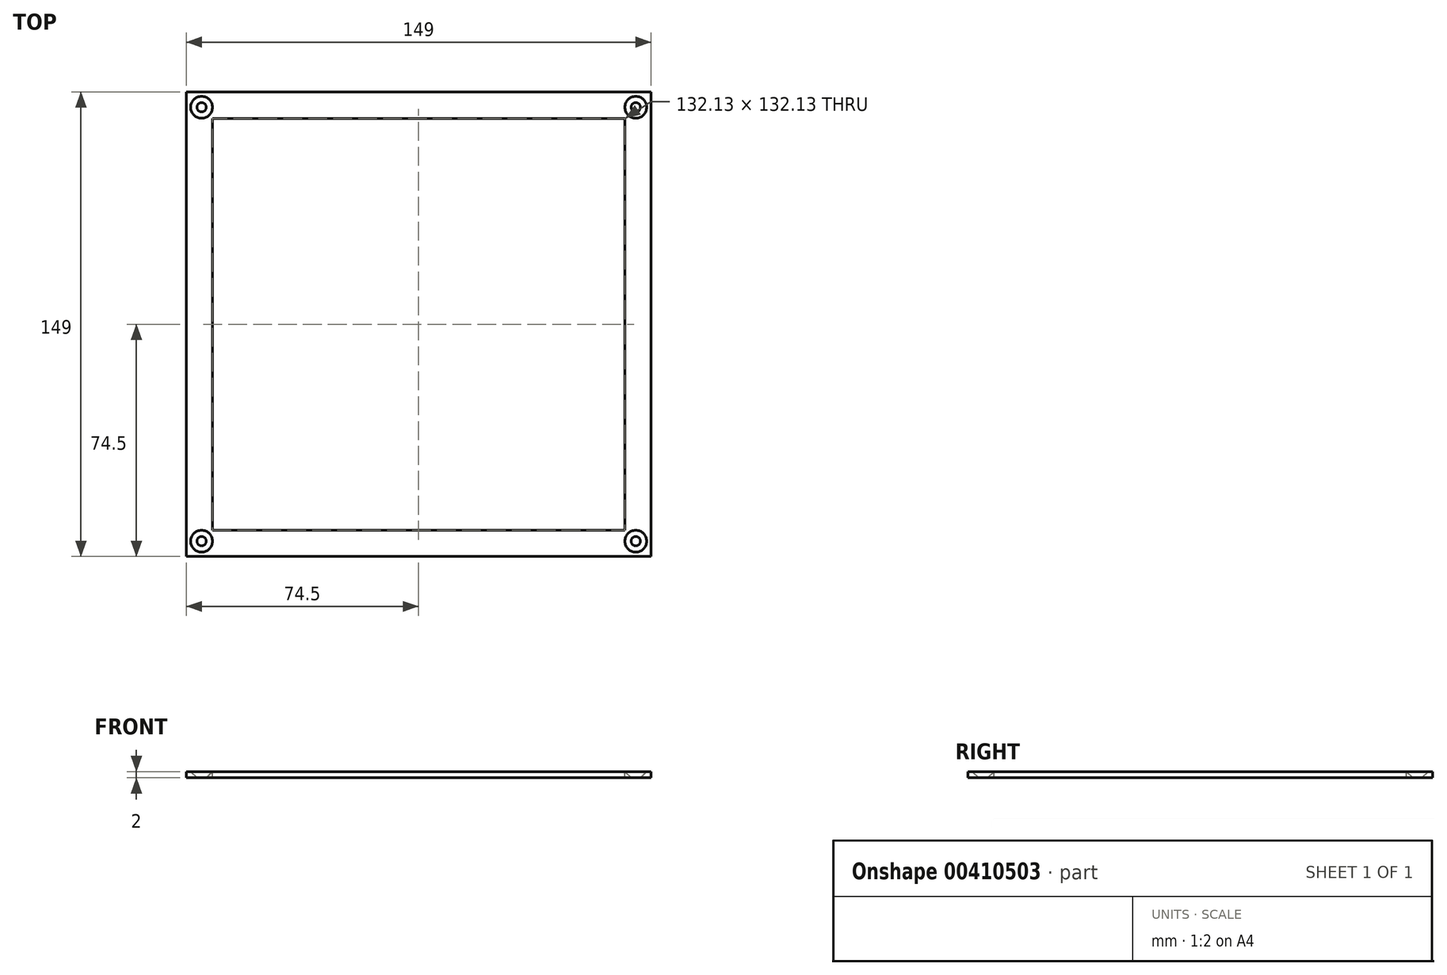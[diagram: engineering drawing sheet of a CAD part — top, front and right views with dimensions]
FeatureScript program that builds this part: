
annotation { "Feature Type Name" : "Feature", "Feature Type Description" : "" }
export const myFeature = defineFeature(function(context is Context, id is Id, definition is map)
    precondition{}
    {
        {
            var Q0;
            Q0=qCreatedBy(makeId("Top.planeOp"),FACE);
            var sketch = newSketch(context, id + "F0", { "sketchPlane" : qUnion([Q0])});
            skLineSegment(sketch, "E0.bottom", {"start": v(60.5, 60.5) * mm, "end": v(-60.5, 60.5) * mm});
            skLineSegment(sketch, "E0.top", {"start": v(60.5, -60.5) * mm, "end": v(-60.5, -60.5) * mm});
            skLineSegment(sketch, "E0.left", {"start": v(60.5, 60.5) * mm, "end": v(60.5, -60.5) * mm});
            skLineSegment(sketch, "E0.right", {"start": v(-60.5, 60.5) * mm, "end": v(-60.5, -60.5) * mm});
            skLineSegment(sketch, "E1.0", {"start": v(60.5, 57.5) * mm, "end": v(-60.5, 57.5) * mm});
            skLineSegment(sketch, "E2.0", {"start": v(57.5, 60.5) * mm, "end": v(57.5, -60.5) * mm});
            skLineSegment(sketch, "E3.0", {"start": v(60.5, -57.5) * mm, "end": v(-60.5, -57.5) * mm});
            skLineSegment(sketch, "E4.0", {"start": v(-57.5, 60.5) * mm, "end": v(-57.5, -60.5) * mm});
            skLineSegment(sketch, "E5.0", {"start": v(60.5, 74.5) * mm, "end": v(-60.5, 74.5) * mm});
            skLineSegment(sketch, "E6.0", {"start": v(60.5, -74.5) * mm, "end": v(-60.5, -74.5) * mm});
            skLineSegment(sketch, "E7.0", {"start": v(-74.5, 60.5) * mm, "end": v(-74.5, -60.5) * mm});
            skLineSegment(sketch, "E8.0", {"start": v(74.5, 60.5) * mm, "end": v(74.5, -60.5) * mm});
            skLineSegment(sketch, "E9", {"start": v(-74.5, 60.5) * mm, "end": v(-74.5, 74.5) * mm});
            skLineSegment(sketch, "E10", {"start": v(-60.5, 74.5) * mm, "end": v(-74.5, 74.5) * mm});
            skLineSegment(sketch, "E11", {"start": v(60.5, 74.5) * mm, "end": v(74.5, 74.5) * mm});
            skLineSegment(sketch, "E12", {"start": v(74.5, 60.5) * mm, "end": v(74.5, 74.5) * mm});
            skLineSegment(sketch, "E13", {"start": v(74.5, -60.5) * mm, "end": v(74.5, -74.5) * mm});
            skLineSegment(sketch, "E14", {"start": v(60.5, -74.5) * mm, "end": v(74.5, -74.5) * mm});
            skLineSegment(sketch, "E15", {"start": v(-60.5, -74.5) * mm, "end": v(-74.5, -74.5) * mm});
            skLineSegment(sketch, "E16", {"start": v(-74.5, -60.5) * mm, "end": v(-74.5, -74.5) * mm});
            skPoint(sketch, "E17.orphan", {"position": v(82.8, 74.5) * mm});
            skSolve(sketch);
        }
        {
            var Q0;
            Q0=makeQuery(id+"F0.imprint","IMPRINT",FACE,{"disambiguationData":[TD([[makeQuery(id+"F0.imprint","IMPRINT",EDGE,{"derivedFrom":sQuery(id+"F0.wireOp",EDGE,"E5.0")}),1.0]])]});
            extrude(context, id + "F1", {"entities" : qUnion([Q0]), "depth" : 5 * mm});
        }
        {
            var Q0;
            {var subQ0=sQuery(id+"F0.wireOp",EDGE,"E2.0");var subQ1=sQuery(id+"F0.wireOp",EDGE,"E0.bottom");var subQ2=makeQuery(id+"F0.imprint","INTERSECT",VERTEX,{"derivedFrom":[subQ1,subQ0]});Q0=makeQuery(id+"F0.imprint","IMPRINT",FACE,{"disambiguationData":[TD([[makeQuery(id+"F0.imprint","IMPRINT",EDGE,{"disambiguationData":[TD([[subQ2,-1.0]])],"derivedFrom":subQ1}),1.0]])]});}
            var Q1;
            {var subQ0=sQuery(id+"F0.wireOp",EDGE,"E0.left");var subQ1=sQuery(id+"F0.wireOp",EDGE,"E0.bottom");var subQ2=makeQuery(id+"F0.imprint","INTERSECT",VERTEX,{"derivedFrom":[subQ1,subQ0]});Q1=makeQuery(id+"F0.imprint","IMPRINT",FACE,{"disambiguationData":[TD([[makeQuery(id+"F0.imprint","IMPRINT",EDGE,{"disambiguationData":[TD([[subQ2,-1.0]])],"derivedFrom":subQ1}),1.0]])]});}
            var Q2;
            {var subQ0=sQuery(id+"F0.wireOp",EDGE,"E1.0");var subQ1=sQuery(id+"F0.wireOp",EDGE,"E0.left");var subQ2=makeQuery(id+"F0.imprint","INTERSECT",VERTEX,{"derivedFrom":[subQ1,subQ0]});Q2=makeQuery(id+"F0.imprint","IMPRINT",FACE,{"disambiguationData":[TD([[makeQuery(id+"F0.imprint","IMPRINT",EDGE,{"disambiguationData":[TD([[subQ2,-1.0]])],"derivedFrom":subQ1}),-1.0]])]});}
            var Q3;
            {var subQ0=sQuery(id+"F0.wireOp",EDGE,"E0.left");var subQ1=sQuery(id+"F0.wireOp",EDGE,"E0.top");var subQ2=makeQuery(id+"F0.imprint","INTERSECT",VERTEX,{"derivedFrom":[subQ1,subQ0]});Q3=makeQuery(id+"F0.imprint","IMPRINT",FACE,{"disambiguationData":[TD([[makeQuery(id+"F0.imprint","IMPRINT",EDGE,{"disambiguationData":[TD([[subQ2,-1.0]])],"derivedFrom":subQ1}),-1.0]])]});}
            var Q4;
            {var subQ0=sQuery(id+"F0.wireOp",EDGE,"E2.0");var subQ1=sQuery(id+"F0.wireOp",EDGE,"E0.top");var subQ2=makeQuery(id+"F0.imprint","INTERSECT",VERTEX,{"derivedFrom":[subQ1,subQ0]});Q4=makeQuery(id+"F0.imprint","IMPRINT",FACE,{"disambiguationData":[TD([[makeQuery(id+"F0.imprint","IMPRINT",EDGE,{"disambiguationData":[TD([[subQ2,-1.0]])],"derivedFrom":subQ1}),-1.0]])]});}
            var Q5;
            {var subQ0=sQuery(id+"F0.wireOp",EDGE,"E1.0");var subQ1=sQuery(id+"F0.wireOp",EDGE,"E0.right");var subQ2=makeQuery(id+"F0.imprint","INTERSECT",VERTEX,{"derivedFrom":[subQ1,subQ0]});Q5=makeQuery(id+"F0.imprint","IMPRINT",FACE,{"disambiguationData":[TD([[makeQuery(id+"F0.imprint","IMPRINT",EDGE,{"disambiguationData":[TD([[subQ2,-1.0]])],"derivedFrom":subQ1}),1.0]])]});}
            var Q6;
            {var subQ0=sQuery(id+"F0.wireOp",EDGE,"E0.right");var subQ1=sQuery(id+"F0.wireOp",EDGE,"E0.top");var subQ2=makeQuery(id+"F0.imprint","INTERSECT",VERTEX,{"derivedFrom":[subQ1,subQ0]});Q6=makeQuery(id+"F0.imprint","IMPRINT",FACE,{"disambiguationData":[TD([[makeQuery(id+"F0.imprint","IMPRINT",EDGE,{"disambiguationData":[TD([[subQ2,1.0]])],"derivedFrom":subQ1}),-1.0]])]});}
            var Q7;
            {var subQ0=sQuery(id+"F0.wireOp",EDGE,"E0.right");var subQ1=sQuery(id+"F0.wireOp",EDGE,"E0.bottom");var subQ2=makeQuery(id+"F0.imprint","INTERSECT",VERTEX,{"derivedFrom":[subQ1,subQ0]});Q7=makeQuery(id+"F0.imprint","IMPRINT",FACE,{"disambiguationData":[TD([[makeQuery(id+"F0.imprint","IMPRINT",EDGE,{"disambiguationData":[TD([[subQ2,1.0]])],"derivedFrom":subQ1}),1.0]])]});}
            extrude(context, id + "F2", {"entities" : qUnion([Q0, Q1, Q2, Q3, Q4, Q5, Q6, Q7]), "operationType" : NewBodyOperationType.ADD, "depth" : 2 * mm});
        }
        {
            var Q0;
            Q0=makeQuery(id+"F1.opExtrude","CAP_FACE",FACE,{"disambiguationData":[OSD([sQuery(id+"F0.wireOp",EDGE,"E0.bottom"),sQuery(id+"F0.wireOp",EDGE,"E0.top"),sQuery(id+"F0.wireOp",EDGE,"E0.left"),sQuery(id+"F0.wireOp",EDGE,"E0.right"),sQuery(id+"F0.wireOp",EDGE,"E5.0"),sQuery(id+"F0.wireOp",EDGE,"E6.0"),sQuery(id+"F0.wireOp",EDGE,"E7.0"),sQuery(id+"F0.wireOp",EDGE,"E8.0"),sQuery(id+"F0.wireOp",EDGE,"E9"),sQuery(id+"F0.wireOp",EDGE,"E10"),sQuery(id+"F0.wireOp",EDGE,"E11"),sQuery(id+"F0.wireOp",EDGE,"E12"),sQuery(id+"F0.wireOp",EDGE,"E13"),sQuery(id+"F0.wireOp",EDGE,"E14"),sQuery(id+"F0.wireOp",EDGE,"E15"),sQuery(id+"F0.wireOp",EDGE,"E16")])],"isStart":false});
            var sketch = newSketch(context, id + "F3", { "sketchPlane" : qUnion([Q0])});
            skCircle(sketch, "E18", {"center": v(42.52, 68.09) * mm, "radius": 2.5 * mm});
            skSolve(sketch);
        }
        {
            var Q0;
            Q0=makeQuery(id+"F3.imprint","IMPRINT",FACE,{"disambiguationData":[TD([[makeQuery(id+"F3.imprint","IMPRINT",EDGE,{"derivedFrom":sQuery(id+"F3.wireOp",EDGE,"E18")}),1.0]])]});
            extrude(context, id + "F4", {"entities" : qUnion([Q0]), "operationType" : NewBodyOperationType.REMOVE, "endBound" : BoundingType.UP_TO_NEXT, "oppositeDirection" : true, "depth" : 25 * mm});
        }
        {
            var Q0;
            Q0=makeQuery(id+"F1.opExtrude","CAP_FACE",FACE,{"disambiguationData":[OSD([sQuery(id+"F0.wireOp",EDGE,"E0.bottom"),sQuery(id+"F0.wireOp",EDGE,"E0.top"),sQuery(id+"F0.wireOp",EDGE,"E0.left"),sQuery(id+"F0.wireOp",EDGE,"E0.right"),sQuery(id+"F0.wireOp",EDGE,"E5.0"),sQuery(id+"F0.wireOp",EDGE,"E6.0"),sQuery(id+"F0.wireOp",EDGE,"E7.0"),sQuery(id+"F0.wireOp",EDGE,"E8.0"),sQuery(id+"F0.wireOp",EDGE,"E9"),sQuery(id+"F0.wireOp",EDGE,"E10"),sQuery(id+"F0.wireOp",EDGE,"E11"),sQuery(id+"F0.wireOp",EDGE,"E12"),sQuery(id+"F0.wireOp",EDGE,"E13"),sQuery(id+"F0.wireOp",EDGE,"E14"),sQuery(id+"F0.wireOp",EDGE,"E15"),sQuery(id+"F0.wireOp",EDGE,"E16")])],"isStart":false});
            var sketch = newSketch(context, id + "F5", { "sketchPlane" : qUnion([Q0])});
            skLineSegment(sketch, "E19.0", {"start": v(60.5, 71.5) * mm, "end": v(71.5, 71.5) * mm});
            skLineSegment(sketch, "E19.1", {"start": v(-71.5, -60.5) * mm, "end": v(-71.5, -71.5) * mm});
            skLineSegment(sketch, "E19.2", {"start": v(-71.5, 60.5) * mm, "end": v(-71.5, -60.5) * mm});
            skLineSegment(sketch, "E19.3", {"start": v(-71.5, 60.5) * mm, "end": v(-71.5, 71.5) * mm});
            skLineSegment(sketch, "E19.4", {"start": v(-60.5, 71.5) * mm, "end": v(-71.5, 71.5) * mm});
            skLineSegment(sketch, "E19.5", {"start": v(-60.5, -71.5) * mm, "end": v(-71.5, -71.5) * mm});
            skLineSegment(sketch, "E19.6", {"start": v(60.5, 71.5) * mm, "end": v(-60.5, 71.5) * mm});
            skLineSegment(sketch, "E19.7", {"start": v(60.5, -71.5) * mm, "end": v(-60.5, -71.5) * mm});
            skLineSegment(sketch, "E19.8", {"start": v(60.5, -71.5) * mm, "end": v(71.5, -71.5) * mm});
            skLineSegment(sketch, "E19.9", {"start": v(71.5, -60.5) * mm, "end": v(71.5, -71.5) * mm});
            skLineSegment(sketch, "E19.10", {"start": v(71.5, 60.5) * mm, "end": v(71.5, -60.5) * mm});
            skLineSegment(sketch, "E19.11", {"start": v(71.5, 60.5) * mm, "end": v(71.5, 71.5) * mm});
            skSolve(sketch);
        }
        {
            var Q0;
            Q0=makeQuery(id+"F5.imprint","IMPRINT",FACE,{"disambiguationData":[TD([[makeQuery(id+"F5.imprint","IMPRINT",EDGE,{"derivedFrom":sQuery(id+"F5.wireOp",EDGE,"E19.0")}),1.0]])]});
            extrude(context, id + "F6", {"entities" : qUnion([Q0]), "operationType" : NewBodyOperationType.ADD, "depth" : 35 * mm});
        }
        {
            var Q0;
            Q0=makeQuery(id+"F6.opExtrude","CAP_FACE",FACE,{"disambiguationData":[OSD([sQuery(id+"F0.wireOp",EDGE,"E5.0"),sQuery(id+"F0.wireOp",EDGE,"E6.0"),sQuery(id+"F0.wireOp",EDGE,"E7.0"),sQuery(id+"F0.wireOp",EDGE,"E8.0"),sQuery(id+"F0.wireOp",EDGE,"E9"),sQuery(id+"F0.wireOp",EDGE,"E10"),sQuery(id+"F0.wireOp",EDGE,"E11"),sQuery(id+"F0.wireOp",EDGE,"E12"),sQuery(id+"F0.wireOp",EDGE,"E13"),sQuery(id+"F0.wireOp",EDGE,"E14"),sQuery(id+"F0.wireOp",EDGE,"E15"),sQuery(id+"F0.wireOp",EDGE,"E16"),sQuery(id+"F5.wireOp",EDGE,"E19.0"),sQuery(id+"F5.wireOp",EDGE,"E19.1"),sQuery(id+"F5.wireOp",EDGE,"E19.2"),sQuery(id+"F5.wireOp",EDGE,"E19.3"),sQuery(id+"F5.wireOp",EDGE,"E19.4"),sQuery(id+"F5.wireOp",EDGE,"E19.5"),sQuery(id+"F5.wireOp",EDGE,"E19.6"),sQuery(id+"F5.wireOp",EDGE,"E19.7"),sQuery(id+"F5.wireOp",EDGE,"E19.8"),sQuery(id+"F5.wireOp",EDGE,"E19.9"),sQuery(id+"F5.wireOp",EDGE,"E19.10"),sQuery(id+"F5.wireOp",EDGE,"E19.11")])],"isStart":false});
            var sketch = newSketch(context, id + "F7", { "sketchPlane" : qUnion([Q0])});
            skCircle(sketch, "E20", {"center": v(-69.6, 69.6) * mm, "radius": 5 * mm});
            skCircle(sketch, "E21", {"center": v(-69.6, 69.6) * mm, "radius": 1.5 * mm});
            skCircle(sketch, "E22.1.0", {"center": v(-69.6, -69.6) * mm, "radius": 5 * mm});
            skCircle(sketch, "E22.1.1", {"center": v(-69.6, -69.6) * mm, "radius": 1.5 * mm});
            skCircle(sketch, "E22.2.0", {"center": v(69.6, -69.6) * mm, "radius": 5 * mm});
            skCircle(sketch, "E22.2.1", {"center": v(69.6, -69.6) * mm, "radius": 1.5 * mm});
            skCircle(sketch, "E22.3.0", {"center": v(69.6, 69.6) * mm, "radius": 5 * mm});
            skCircle(sketch, "E22.3.1", {"center": v(69.6, 69.6) * mm, "radius": 1.5 * mm});
            skPoint(sketch, "E22.center", {"position": v(0, 0) * mm});
            skSolve(sketch);
        }
        {
            var Q0;
            Q0=makeQuery(id+"F7.imprint","IMPRINT",FACE,{"disambiguationData":[TD([[makeQuery(id+"F7.imprint","IMPRINT",EDGE,{"derivedFrom":sQuery(id+"F7.wireOp",EDGE,"E21")}),-1.0]])]});
            var Q1;
            Q1=makeQuery(id+"F7.imprint","IMPRINT",FACE,{"disambiguationData":[TD([[makeQuery(id+"F7.imprint","IMPRINT",EDGE,{"derivedFrom":sQuery(id+"F7.wireOp",EDGE,"E22.3.1")}),-1.0]])]});
            var Q2;
            Q2=makeQuery(id+"F7.imprint","IMPRINT",FACE,{"disambiguationData":[TD([[makeQuery(id+"F7.imprint","IMPRINT",EDGE,{"derivedFrom":sQuery(id+"F7.wireOp",EDGE,"E22.2.1")}),-1.0]])]});
            var Q3;
            Q3=makeQuery(id+"F7.imprint","IMPRINT",FACE,{"disambiguationData":[TD([[makeQuery(id+"F7.imprint","IMPRINT",EDGE,{"derivedFrom":sQuery(id+"F7.wireOp",EDGE,"E22.1.1")}),-1.0]])]});
            extrude(context, id + "F8", {"entities" : qUnion([Q0, Q1, Q2, Q3]), "operationType" : NewBodyOperationType.ADD, "oppositeDirection" : true, "depth" : 35 * mm});
        }
        {
            var Q0;
            {var subQ0=sQuery(id+"F0.wireOp",EDGE,"E15");var subQ1=sQuery(id+"F0.wireOp",EDGE,"E14");var subQ2=sQuery(id+"F0.wireOp",EDGE,"E6.0");Q0=makeQuery(id+"F6.boolean.opBoolean","MERGE",FACE,{"derivedFrom":[makeQuery(id+"F1.opExtrude","SWEPT_FACE",FACE,{"disambiguationData":[OSD([subQ2,subQ1,subQ0])]}),makeQuery(id+"F6.opExtrude","SWEPT_FACE",FACE,{"disambiguationData":[OSD([subQ2,subQ1,subQ0])]})]});}
            var sketch = newSketch(context, id + "F9", { "sketchPlane" : qUnion([Q0])});
            skLineSegment(sketch, "E23.0", {"start": v(74.5, 38) * mm, "end": v(-74.5, 38) * mm});
            skLineSegment(sketch, "E24", {"start": v(-74.5, 38) * mm, "end": v(-74.5, -12.58) * mm});
            skLineSegment(sketch, "E25", {"start": v(-74.5, -12.58) * mm, "end": v(74.5, -12.58) * mm});
            skLineSegment(sketch, "E26", {"start": v(74.5, -12.58) * mm, "end": v(74.5, 38) * mm});
            skSolve(sketch);
        }
        {
            var Q0;
            Q0 = qSketchRegion(id + "F9", true);
            extrude(context, id + "F10", {"entities" : qUnion([Q0]), "operationType" : NewBodyOperationType.REMOVE, "oppositeDirection" : true, "depth" : 200 * mm});
        }
        {
            var Q0;
            {var subQ0=sQuery(id+"F5.wireOp",EDGE,"E19.11");var subQ1=sQuery(id+"F5.wireOp",EDGE,"E19.10");var subQ2=sQuery(id+"F5.wireOp",EDGE,"E19.9");var subQ3=sQuery(id+"F5.wireOp",EDGE,"E19.6");var subQ4=sQuery(id+"F5.wireOp",EDGE,"E19.4");var subQ5=sQuery(id+"F5.wireOp",EDGE,"E19.0");var subQ6=sQuery(id+"F5.wireOp",EDGE,"E19.8");var subQ7=sQuery(id+"F5.wireOp",EDGE,"E19.7");var subQ8=sQuery(id+"F5.wireOp",EDGE,"E19.5");var subQ9=sQuery(id+"F5.wireOp",EDGE,"E19.3");var subQ10=sQuery(id+"F5.wireOp",EDGE,"E19.2");var subQ11=sQuery(id+"F5.wireOp",EDGE,"E19.1");Q0=makeQuery(id+"F8.boolean.opBoolean","MERGE",FACE,{"derivedFrom":[makeQuery(id+"F6.opExtrude","CAP_FACE",FACE,{"disambiguationData":[OSD([sQuery(id+"F0.wireOp",EDGE,"E5.0"),sQuery(id+"F0.wireOp",EDGE,"E6.0"),sQuery(id+"F0.wireOp",EDGE,"E7.0"),sQuery(id+"F0.wireOp",EDGE,"E8.0"),sQuery(id+"F0.wireOp",EDGE,"E9"),sQuery(id+"F0.wireOp",EDGE,"E10"),sQuery(id+"F0.wireOp",EDGE,"E11"),sQuery(id+"F0.wireOp",EDGE,"E12"),sQuery(id+"F0.wireOp",EDGE,"E13"),sQuery(id+"F0.wireOp",EDGE,"E14"),sQuery(id+"F0.wireOp",EDGE,"E15"),sQuery(id+"F0.wireOp",EDGE,"E16"),subQ5,subQ11,subQ10,subQ9,subQ4,subQ8,subQ3,subQ7,subQ6,subQ2,subQ1,subQ0])],"isStart":false}),makeQuery(id+"F8.opExtrude","CAP_FACE",FACE,{"disambiguationData":[OSD([subQ5,subQ11,subQ10,subQ9,subQ4,subQ3,sQuery(id+"F7.wireOp",EDGE,"E20"),sQuery(id+"F7.wireOp",EDGE,"E21")])],"isStart":true}),makeQuery(id+"F8.opExtrude","CAP_FACE",FACE,{"disambiguationData":[OSD([subQ11,subQ10,subQ9,subQ8,subQ7,subQ6,sQuery(id+"F7.wireOp",EDGE,"E22.1.0"),sQuery(id+"F7.wireOp",EDGE,"E22.1.1")])],"isStart":true}),makeQuery(id+"F8.opExtrude","CAP_FACE",FACE,{"disambiguationData":[OSD([subQ8,subQ7,subQ6,subQ2,subQ1,subQ0,sQuery(id+"F7.wireOp",EDGE,"E22.2.0"),sQuery(id+"F7.wireOp",EDGE,"E22.2.1")])],"isStart":true}),makeQuery(id+"F8.opExtrude","CAP_FACE",FACE,{"disambiguationData":[OSD([subQ5,subQ4,subQ3,subQ2,subQ1,subQ0,sQuery(id+"F7.wireOp",EDGE,"E22.3.0"),sQuery(id+"F7.wireOp",EDGE,"E22.3.1")])],"isStart":true})]});}
            var sketch = newSketch(context, id + "F11", { "sketchPlane" : qUnion([Q0])});
            skLineSegment(sketch, "E27", {"start": v(-66.06, 66.06) * mm, "end": v(-66.06, -66.06) * mm});
            skLineSegment(sketch, "E28", {"start": v(-66.06, -66.06) * mm, "end": v(66.06, -66.06) * mm});
            skLineSegment(sketch, "E29", {"start": v(66.06, -66.06) * mm, "end": v(66.06, 66.06) * mm});
            skLineSegment(sketch, "E30", {"start": v(66.06, 66.06) * mm, "end": v(-66.06, 66.06) * mm});
            skSolve(sketch);
        }
        {
            var Q0;
            {var subQ0=sQuery(id+"F11.wireOp",EDGE,"E30");Q0=makeQuery(id+"F11.imprint","IMPRINT",FACE,{"disambiguationData":[TD([[makeQuery(id+"F11.imprint","IMPRINT",EDGE,{"derivedFrom":subQ0}),-1.0]])]});}
            var Q1;
            {var subQ0=sQuery(id+"F11.wireOp",EDGE,"E29");Q1=makeQuery(id+"F11.imprint","IMPRINT",FACE,{"disambiguationData":[TD([[makeQuery(id+"F11.imprint","IMPRINT",EDGE,{"derivedFrom":subQ0}),-1.0]])]});}
            var Q2;
            {var subQ0=sQuery(id+"F11.wireOp",EDGE,"E28");Q2=makeQuery(id+"F11.imprint","IMPRINT",FACE,{"disambiguationData":[TD([[makeQuery(id+"F11.imprint","IMPRINT",EDGE,{"derivedFrom":subQ0}),-1.0]])]});}
            var Q3;
            {var subQ0=sQuery(id+"F11.wireOp",EDGE,"E27");Q3=makeQuery(id+"F11.imprint","IMPRINT",FACE,{"disambiguationData":[TD([[makeQuery(id+"F11.imprint","IMPRINT",EDGE,{"derivedFrom":subQ0}),-1.0]])]});}
            extrude(context, id + "F12", {"entities" : qUnion([Q0, Q1, Q2, Q3]), "operationType" : NewBodyOperationType.ADD, "oppositeDirection" : true, "depth" : 2 * mm});
        }
        {
            var Q0;
            Q0=makeQuery(id+"F8.opExtrude","CAP_EDGE",EDGE,{"disambiguationData":[OSD([sQuery(id+"F7.wireOp",EDGE,"E21")])],"isStart":true});
            var Q1;
            Q1=makeQuery(id+"F8.opExtrude","CAP_EDGE",EDGE,{"disambiguationData":[OSD([sQuery(id+"F7.wireOp",EDGE,"E22.3.1")])],"isStart":true});
            var Q2;
            Q2=makeQuery(id+"F8.opExtrude","CAP_EDGE",EDGE,{"disambiguationData":[OSD([sQuery(id+"F7.wireOp",EDGE,"E22.2.1")])],"isStart":true});
            var Q3;
            Q3=makeQuery(id+"F8.opExtrude","CAP_EDGE",EDGE,{"disambiguationData":[OSD([sQuery(id+"F7.wireOp",EDGE,"E22.1.1")])],"isStart":true});
            chamfer(context, id + "F13", {"entities" : qUnion([Q0, Q1, Q2, Q3]), "width" : 2 * mm, "tangentPropagation" : true});
        }
    });
